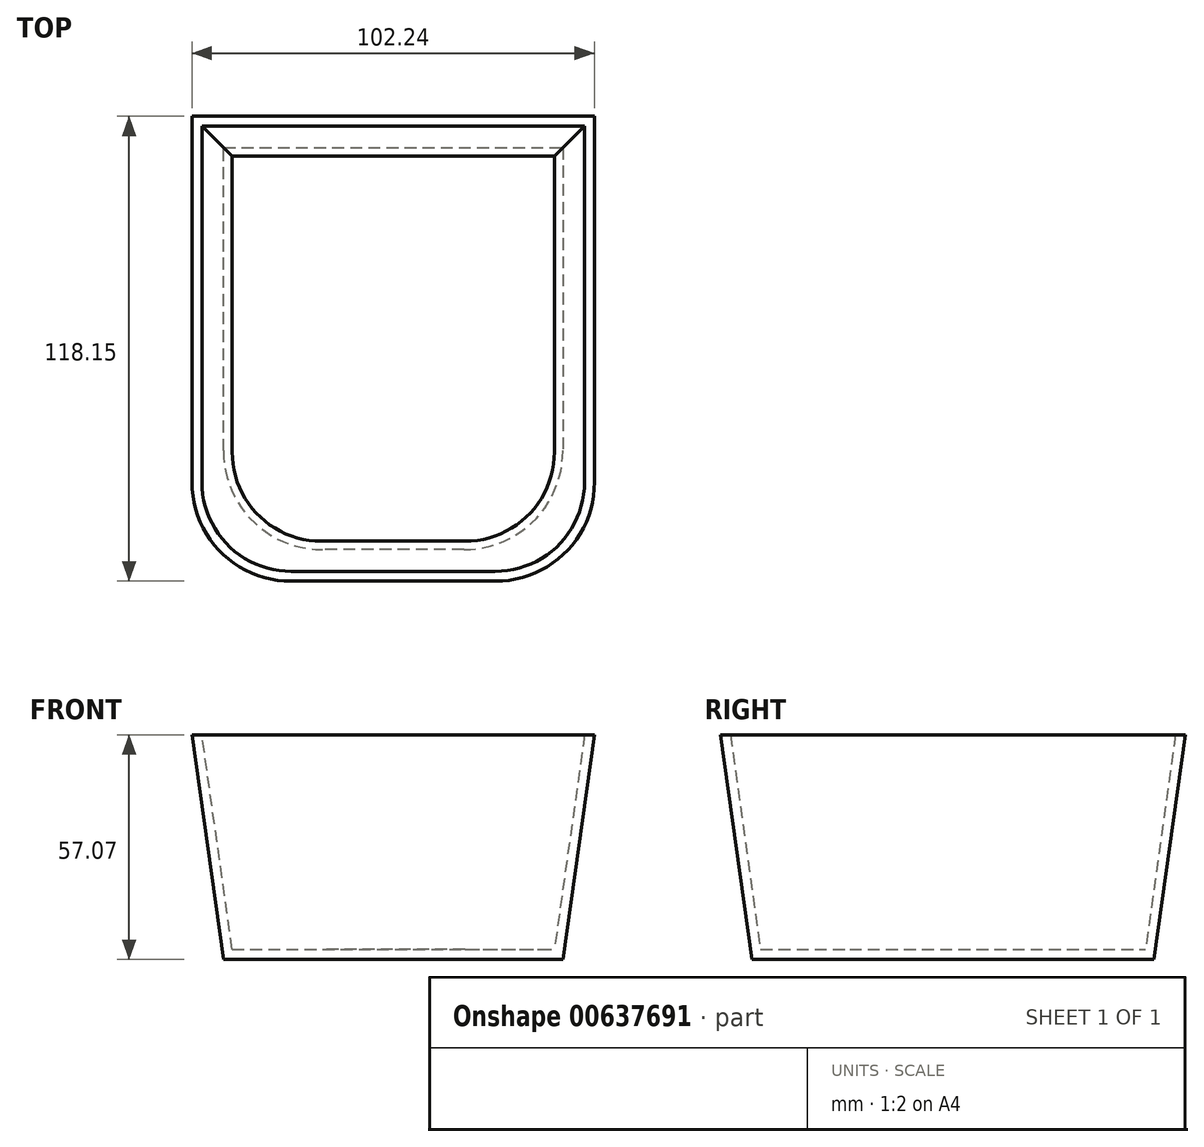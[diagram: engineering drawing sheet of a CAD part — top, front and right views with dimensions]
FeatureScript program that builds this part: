
annotation { "Feature Type Name" : "Feature", "Feature Type Description" : "" }
export const myFeature = defineFeature(function(context is Context, id is Id, definition is map)
    precondition{}
    {
        {
            var Q0;
            Q0=qCreatedBy(makeId("Top.planeOp"),FACE);
            var sketch = newSketch(context, id + "F0", { "sketchPlane" : qUnion([Q0])});
            skLineSegment(sketch, "E0.bottom", {"start": v(-36.75, 88.42) * mm, "end": v(49.45, 88.42) * mm});
            skLineSegment(sketch, "E0.top", {"start": v(-36.75, -13.7) * mm, "end": v(49.45, -13.7) * mm});
            skLineSegment(sketch, "E0.left", {"start": v(-36.75, 88.42) * mm, "end": v(-36.75, -13.7) * mm});
            skLineSegment(sketch, "E0.right", {"start": v(49.45, 88.42) * mm, "end": v(49.45, -13.7) * mm});
            skPoint(sketch, "E0.middle", {"position": v(6.35, 37.37) * mm});
            skSolve(sketch);
        }
        {
            var Q0;
            Q0 = qSketchRegion(id + "F0", true);
            extrude(context, id + "F1", {"entities" : qUnion([Q0]), "depth" : 57.07 * mm, "offsetDistance" : 25.4 * mm, "hasDraft" : true, "draftAngle" : 8 * degree});
        }
        {
            var Q0;
            Q0=makeQuery(id+"F1.opExtrude","SWEPT_EDGE",EDGE,{"disambiguationData":[OSD([sQuery(id+"F0.wireOp",EDGE,"E0.top"),sQuery(id+"F0.wireOp",EDGE,"E0.right")])]});
            var Q1;
            Q1=makeQuery(id+"F1.opExtrude","SWEPT_EDGE",EDGE,{"disambiguationData":[OSD([sQuery(id+"F0.wireOp",EDGE,"E0.top"),sQuery(id+"F0.wireOp",EDGE,"E0.left")])]});
            fillet(context, id + "F2", {"entities" : qUnion([Q0, Q1]), "radius" : 25.4 * mm, "tangentPropagation" : true, "allowEdgeOverflow" : false});
        }
        {
            var Q0;
            Q0=makeQuery(id+"F1.opExtrude","CAP_FACE",FACE,{"disambiguationData":[OSD([sQuery(id+"F0.wireOp",EDGE,"E0.bottom"),sQuery(id+"F0.wireOp",EDGE,"E0.top"),sQuery(id+"F0.wireOp",EDGE,"E0.left"),sQuery(id+"F0.wireOp",EDGE,"E0.right")])],"isStart":false});
            shell(context, id + "F3", {"entities" : qUnion([Q0]), "thickness" : 2.5 * mm});
        }
    });
